# Revit family: Triturador_XM-51_GENERADO
name_source: partatom
category: Equipos especializados
revit_build: Autodesk Revit 2016 (Build: 20151007_0715(x64)
units: mm (PartAtom-declared; Revit-internal decimal feet)

## family parameters
Compartido = No
Corte con vacíos al cargar = No
Cota de conector redondo = Diámetro de uso
Número OmniClass = 23.21.21.31.11
Punto de cálculo de habitación = No
Se basa en plano de trabajo = No
Siempre vertical = Sí
Tipo de pieza = Normal

## types (6) — shared parameters
Cycle = 50 Hz
Fabricante = SAMMIC S.L.
Foodservice Equipment Identifier = Sí
Phase = 1
Revision Code = 1
URL = https://www.sammic.com
URL Cutsheet = http://www.sammic.com

## per-type parameters (varying)
| type | Comentarios de tipo | FL Amps | Modelo | Specification by Manufacturer | Volts | Weight in Pounds |
| Immersion blender XM-51 230/50-60/1 | Professional immersion blender. 570 W. | 3 A | 3030820 | Fixed speed motor block.
420 mm detachable arm.
Designed for continuous use in recipients of up to 80 litres. | 230 V | 10.6 |
| Immersion blender XM-51 230/50-60/1 AUS | Professional immersion blender. 570 W. | 3 A | 3030822 | Fixed speed motor block.
420 mm detachable arm.
Designed for continuous use in recipients of up to 80 litres. | 230 V | 10.6 |
| Immersion blender XM-51 120/50-60/1 USA | Professional immersion blender. 570 W. | 4 A | 3030825 | Fixed speed motor block.
420 mm detachable arm.
Designed for continuous use in recipients of up to 80 litres. | 120 V | 10.6 |
| Immersion blender & whisk combo MB-51 230/50-60/1 | Professional hand blender and beater. 570 W. | 3 A | 3030826 | Variable speed motor block.
420 mm detachable mixer arm designed for continuous use in recipients of up to 80 litres.
Whisk with capacity for 2 to 80 egg whites. | 230 V | 10.3 |
| Immersion blender & whisk combo MB-51 230/50-60/1 AUS | Professional hand blender and beater. 570 W. | 3 A | 3030828 | Variable speed motor block.
420 mm detachable mixer arm designed for continuous use in recipients of up to 80 litres.
Whisk with capacity for 2 to 80 egg whites. | 230 V | 10.3 |
| Immersion blender & whisk combo MB-51 120/50-60/1 USA | Professional hand blender and beater. 570 W. | 4 A | 3030831 | Variable speed motor block.
420 mm detachable mixer arm designed for continuous use in recipients of up to 80 litres.
Whisk with capacity for 2 to 80 egg whites. | 120 V | 10.3 |

note: column(s) folded — value = type name in every type: Descripción
